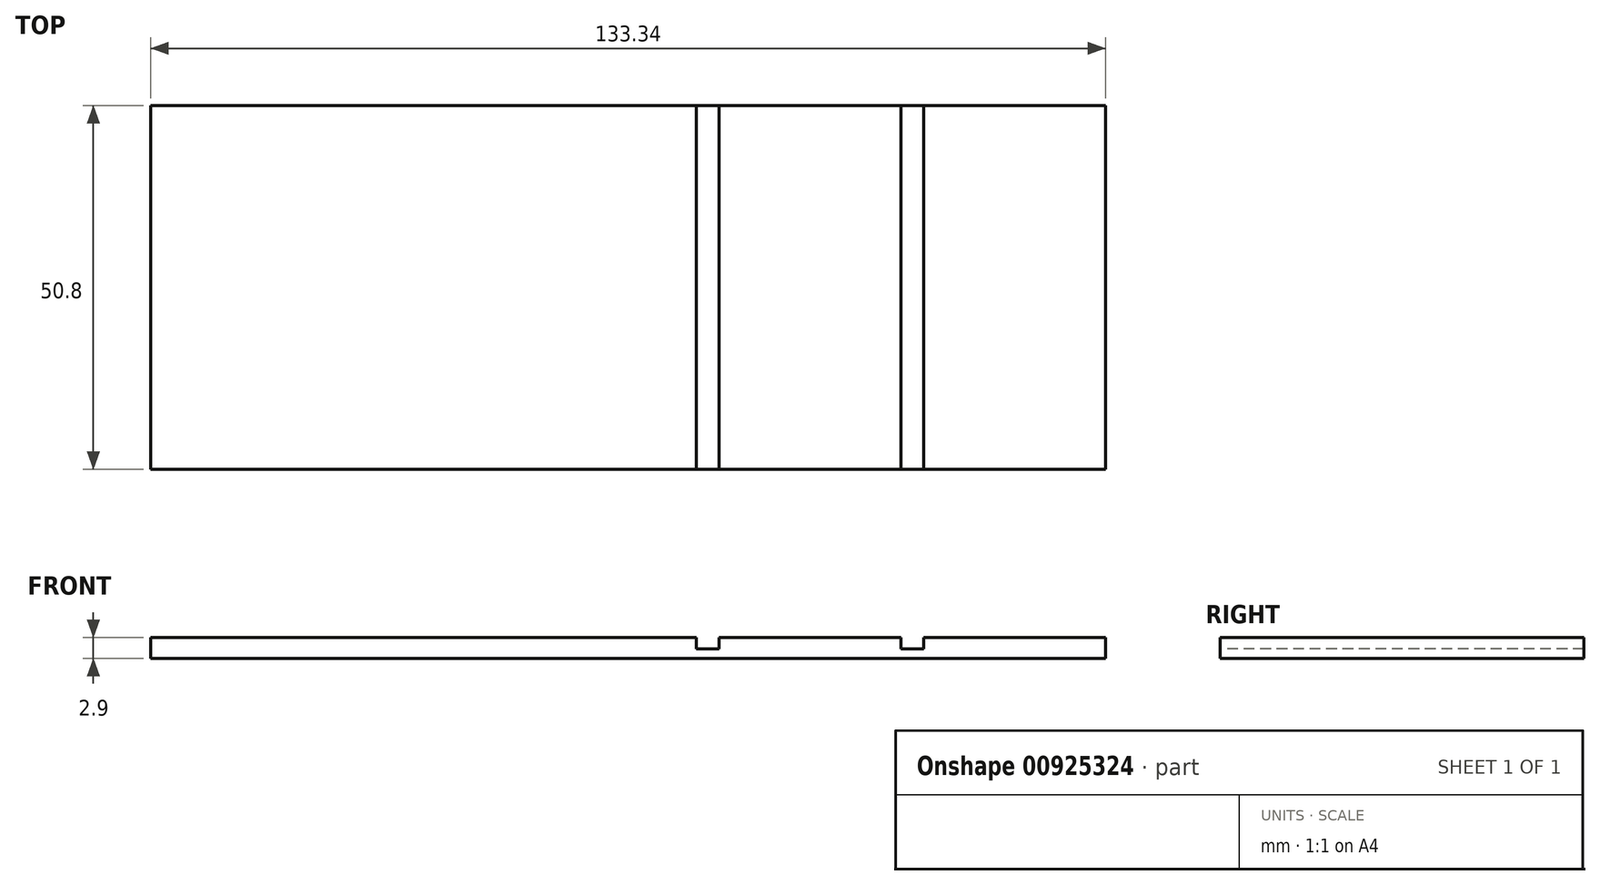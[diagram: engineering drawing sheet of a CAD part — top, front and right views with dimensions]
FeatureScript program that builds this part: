
annotation { "Feature Type Name" : "Feature", "Feature Type Description" : "" }
export const myFeature = defineFeature(function(context is Context, id is Id, definition is map)
    precondition{}
    {
        {
            var Q0;
            Q0=qCreatedBy(makeId("Top.planeOp"),FACE);
            var sketch = newSketch(context, id + "F0", { "sketchPlane" : qUnion([Q0])});
            skLineSegment(sketch, "E0.bottom", {"start": v(66.68, -25.4) * mm, "end": v(-66.67, -25.4) * mm});
            skLineSegment(sketch, "E0.top", {"start": v(66.68, 25.4) * mm, "end": v(-66.68, 25.4) * mm});
            skLineSegment(sketch, "E0.left", {"start": v(66.68, -25.4) * mm, "end": v(66.68, 25.4) * mm});
            skLineSegment(sketch, "E0.right", {"start": v(-66.67, -25.4) * mm, "end": v(-66.68, 25.4) * mm});
            skPoint(sketch, "E0.middle", {"position": v(0, 0) * mm});
            skSolve(sketch);
        }
        {
            var Q0;
            Q0=qSketchRegion(id+"F0",true);
            extrude(context, id + "F1", {"entities" : qUnion([Q0]), "depth" : 2.9 * mm, "offsetDistance" : 25.4 * mm});
        }
        {
            var Q0;
            Q0=makeQuery(id+"F1.opExtrude","CAP_FACE",FACE,{"disambiguationData":[OSD([sQuery(id+"F0.wireOp",EDGE,"E0.bottom"),sQuery(id+"F0.wireOp",EDGE,"E0.top"),sQuery(id+"F0.wireOp",EDGE,"E0.left"),sQuery(id+"F0.wireOp",EDGE,"E0.right")])],"isStart":false});
            var sketch = newSketch(context, id + "F2", { "sketchPlane" : qUnion([Q0])});
            skLineSegment(sketch, "E1.bottom", {"start": v(41.28, 25.4) * mm, "end": v(38.1, 25.4) * mm});
            skLineSegment(sketch, "E1.top", {"start": v(41.28, -25.4) * mm, "end": v(38.1, -25.4) * mm});
            skLineSegment(sketch, "E1.left", {"start": v(41.28, 25.4) * mm, "end": v(41.28, -25.4) * mm});
            skLineSegment(sketch, "E1.right", {"start": v(38.1, 25.4) * mm, "end": v(38.1, -25.4) * mm});
            skLineSegment(sketch, "E2.bottom", {"start": v(9.53, 25.4) * mm, "end": v(12.7, 25.4) * mm});
            skLineSegment(sketch, "E2.top", {"start": v(9.53, -25.4) * mm, "end": v(12.7, -25.4) * mm});
            skLineSegment(sketch, "E2.left", {"start": v(9.53, 25.4) * mm, "end": v(9.53, -25.4) * mm});
            skLineSegment(sketch, "E2.right", {"start": v(12.7, 25.4) * mm, "end": v(12.7, -25.4) * mm});
            skSolve(sketch);
        }
        {
            var Q0;
            Q0 = qSketchRegion(id + "F2", true);
            extrude(context, id + "F3", {"entities" : qUnion([Q0]), "operationType" : NewBodyOperationType.REMOVE, "oppositeDirection" : true, "depth" : 1.59 * mm, "offsetDistance" : 25.4 * mm});
        }
    });
